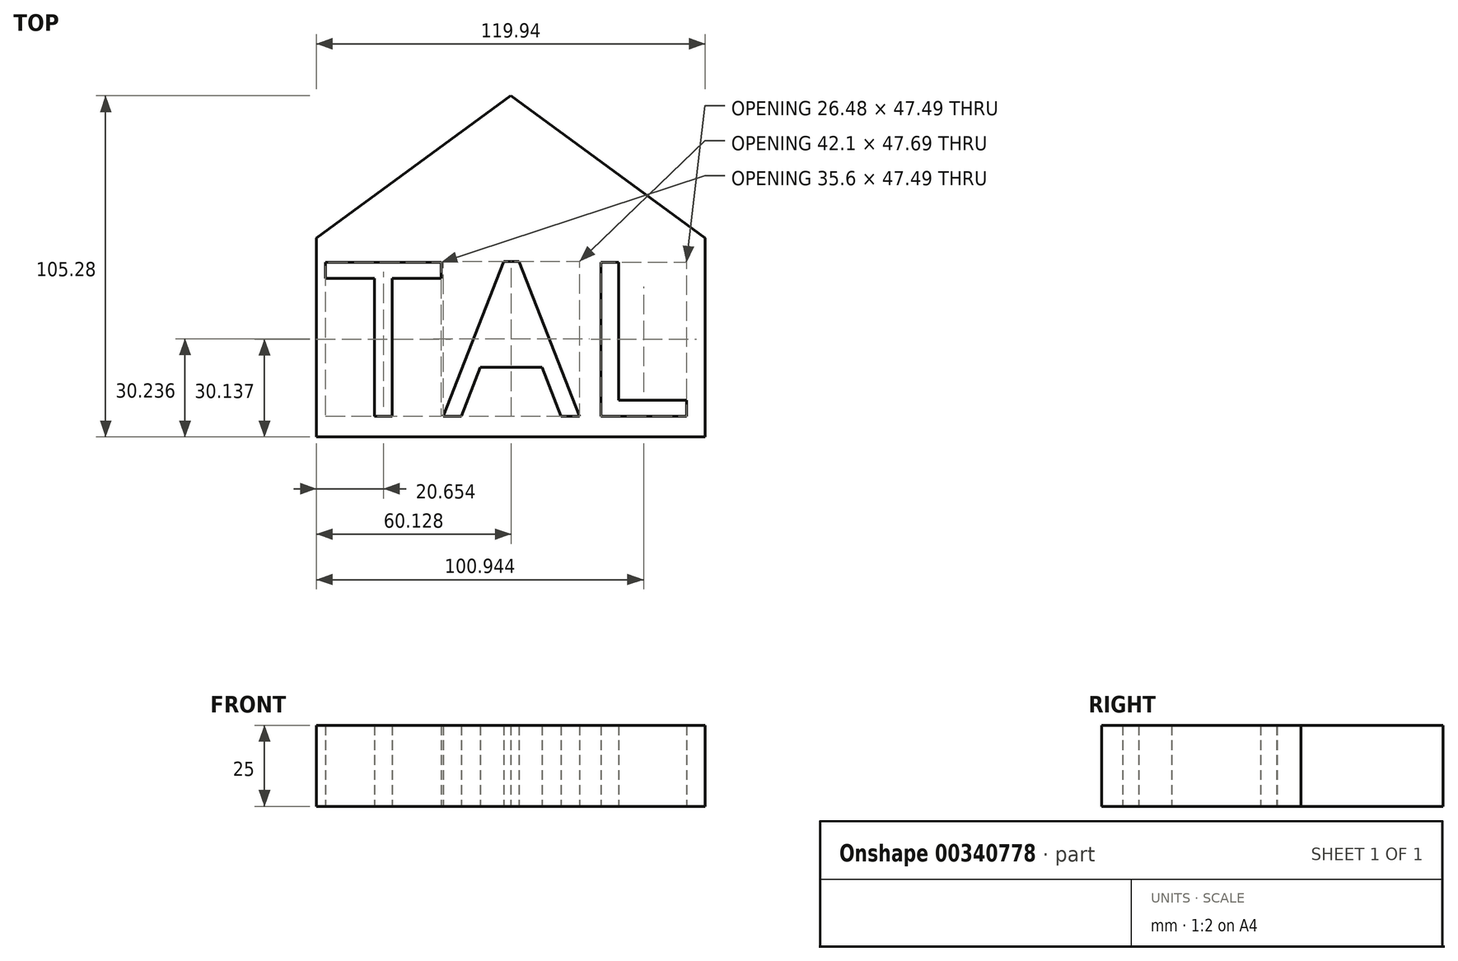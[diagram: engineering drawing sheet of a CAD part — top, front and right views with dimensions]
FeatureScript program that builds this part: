
annotation { "Feature Type Name" : "Feature", "Feature Type Description" : "" }
export const myFeature = defineFeature(function(context is Context, id is Id, definition is map)
    precondition{}
    {
        {
            var Q0;
            Q0=qCreatedBy(makeId("Top.planeOp"),FACE);
            var sketch = newSketch(context, id + "F0", { "sketchPlane" : qUnion([Q0])});
            skLineSegment(sketch, "E0.bottom", {"start": v(59.97, 30.7) * mm, "end": v(-59.97, 30.7) * mm});
            skLineSegment(sketch, "E0.top", {"start": v(59.97, -30.7) * mm, "end": v(-59.97, -30.7) * mm});
            skLineSegment(sketch, "E0.left", {"start": v(59.97, 30.7) * mm, "end": v(59.97, -30.7) * mm});
            skLineSegment(sketch, "E0.right", {"start": v(-59.97, 30.7) * mm, "end": v(-59.97, -30.7) * mm});
            skPoint(sketch, "E0.middle", {"position": v(0, 0) * mm});
            skLineSegment(sketch, "E1", {"start": v(-59.97, 30.7) * mm, "end": v(0, 74.58) * mm});
            skLineSegment(sketch, "E2", {"start": v(0, 74.58) * mm, "end": v(59.97, 30.7) * mm});
            skText(sketch, "E3", { "text": "TAL\n", "fontName": "OpenSans-Regular.ttf"});
            const initialGuessF0  = {"E3": [-0.0577, -0.02431, 1, 0, 0.0479]};
            skSetInitialGuess(sketch, initialGuessF0);
            skSolve(sketch);
        }
        {
            var Q0;
            Q0=makeQuery(id+"F0.imprint","IMPRINT",FACE,{"disambiguationData":[TD([[makeQuery(id+"F0.imprint","IMPRINT",EDGE,{"derivedFrom":sQuery(id+"F0.wireOp",EDGE,"E0.bottom")}),-1.0]])]});
            extrude(context, id + "F1", {"entities" : qUnion([Q0]), "depth" : 25 * mm});
        }
        {
            var Q0;
            Q0 = qSketchRegion(id + "F0", true);
            extrude(context, id + "F2", {"entities" : qUnion([Q0]), "operationType" : NewBodyOperationType.ADD, "depth" : 25 * mm});
        }
        {
            var Q0;
            Q0=makeQuery(id+"F0.imprint","IMPRINT",FACE,{"disambiguationData":[TD([[makeQuery(id+"F0.imprint","IMPRINT",EDGE,{"derivedFrom":sQuery(id+"F0.wireOp",EDGE,"E0.bottom")}),1.0]])]});
            extrude(context, id + "F3", {"entities" : qUnion([Q0]), "operationType" : NewBodyOperationType.ADD, "depth" : 25 * mm});
        }
    });
